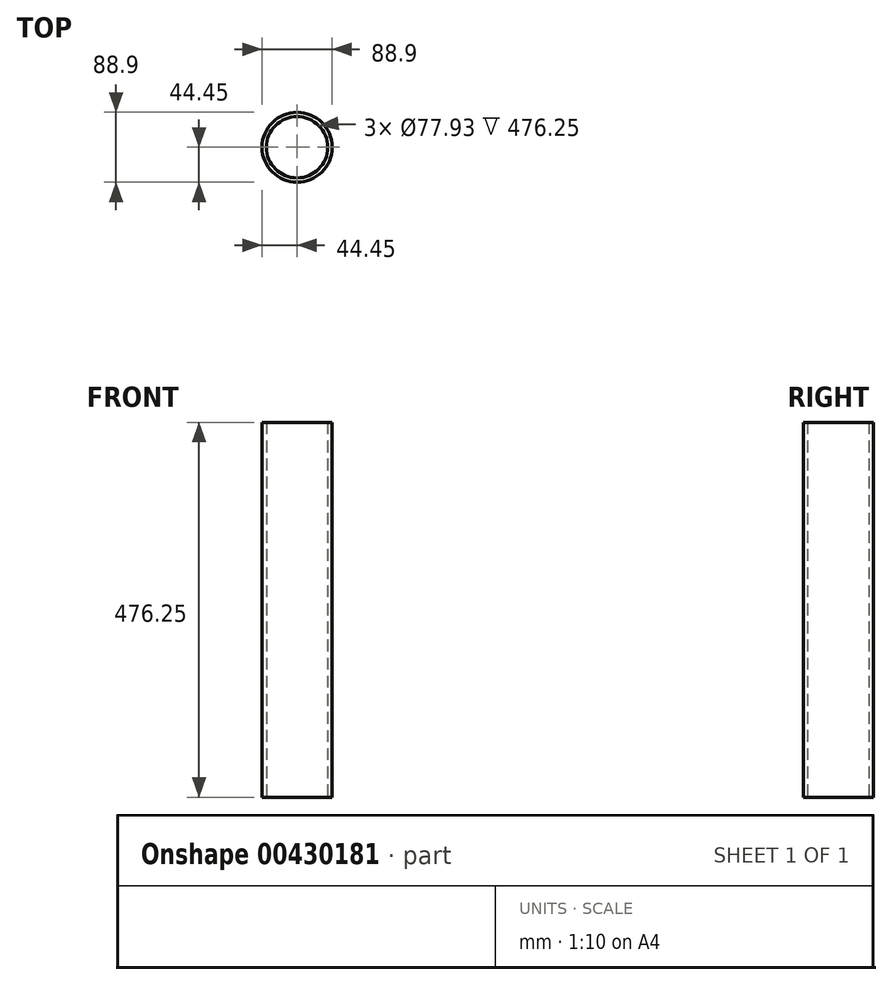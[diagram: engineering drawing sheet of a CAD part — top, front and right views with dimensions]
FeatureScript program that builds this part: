
annotation { "Feature Type Name" : "Feature", "Feature Type Description" : "" }
export const myFeature = defineFeature(function(context is Context, id is Id, definition is map)
    precondition{}
    {
        {
            var Q0;
            Q0=qCreatedBy(makeId("Top.planeOp"),FACE);
            var sketch = newSketch(context, id + "F0", { "sketchPlane" : qUnion([Q0])});
            skCircle(sketch, "E0", {"center": v(0, 0) * mm, "radius": 44.45 * mm});
            skCircle(sketch, "E1", {"center": v(0, 0) * mm, "radius": 38.96 * mm});
            skSolve(sketch);
        }
        {
            var Q0;
            Q0 = qSketchRegion(id + "F0", true);
            extrude(context, id + "F1", {"entities" : qUnion([Q0]), "depth" : 476.25 * mm});
        }
    });
